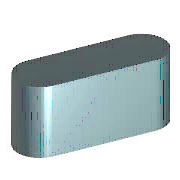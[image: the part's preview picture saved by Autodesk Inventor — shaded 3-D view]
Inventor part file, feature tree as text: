
AUTODESK INVENTOR PART (.ipt)
format: ipt  version: 2025 (Build 290162000, 162)  size: 123,904 bytes
history: native  units: mm (DEFAULTED — no unit token found)
features: plane x3, extrude x1
ambient origin geometry x8: Origin, YZ Plane, XZ Plane, XY Plane, X Axis, Y Axis, Z Axis, Center Point
bodies: Solid1 (feature_tree)
feature tree (4):
  plane  "Work Plane1"
  plane  "Work Plane2"
  extrude  "轴承体1"  Depth=9.0mm
  plane  "Work Plane3"
